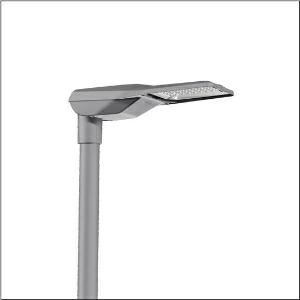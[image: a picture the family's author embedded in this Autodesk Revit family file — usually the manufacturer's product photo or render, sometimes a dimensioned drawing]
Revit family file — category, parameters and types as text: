
# Revit family: streetlight_sl_21_iq_mini___st0_8a_5xe2c31d08jb_69b6
name_source: partatom
category: Lighting Fixtures
units: mm (PartAtom-declared; Revit-internal decimal feet)

## family parameters
Cut with Voids When Loaded = No
Host = Face
Light Source = No
Part Type = Normal
Room Calculation Point = No
Round Connector Dimension = Use Diameter
Shared = No

## types (1)
- --- (1 x LED, 10820 lm, 71.6 W, 3000K)
    Apparent Load = 72 VA
    CIE Flux Codes = 41 75 97 100 100
    Color Rendering = 70
    Color Temperature = 3000K
    Default Elevation = 1800 mm
    Description = Streetlight SL 21 iQ mini, mast luminaire, primary light control with lens, of PMMA, primary optical cover: cover, of toughened safety glass, transparent, light distribution: ST0.8a, light emission: direct distribution, primary light characteristic: asymmetric, installation type: post-top, side-entry, LED, High Power LED, rated luminous flux: 10.820lm, luminous efficacy: 151lm/W, light colour: 730, colour temperature: 3000K, control: Auto-Match, Temp-Guard, Lumen-Switch, Night-Set, Smart-Wire, Light-Fading, Desk-Remote (wireless, voltage-free reading and setting of iQ features in the workshop via application-optimized NFC function/RFID function), optimised constant luminous flux control (CLO 2.0), pre-setting: linear dimming characteristic, mains connection: 220..240V, AC, 50/60Hz, start of lifetime: 72W, end of service life: 75W, reduction: 33W, luminaire housing, of diecast aluminium, powder-coated, Siteco® metallic grey (DB 702S), corrosivity category C5 mid according to DIN EN ISO 12944, please order mast flange separately, inclination adjustable: 0°, 5°, 10°, 15°, sealing non-destructively replaceable, multi-level sealing system, length: 628mm, width: 235mm, height: 110mm, mast flange for spigot size: 42mm (side-entry): 5XC10008XM4, 60/48mm (side-entry/post-top): 5XC10108XM2, 76/60mm (side-entry/post-top): 5XC10108XM1, protection rating (complete): IP66, insulation class (complete): insulation class II (safety insulation), certification: CE, ENEC, ENEC+, VDE, impact resistance: IK09, permissible operating ambient temperature for outdoor applications: -40..+50°C, standard-compliant lighting for roads and squares, packaging unit: 1 piece

Light Distribution: ST0.8a
    Height = 110 mm
    Lamp = 1 x LED
    Lamp Light Flux = 10820 lm
    Lamp Power = 71.6 W
    Lamp count = 1
    Length = 625 mm
    Luminous efficacy = 151 lm/W
    Manufacturer = Siteco
    ModVariant = No
    Model = 5XE2C31D08JB
    Number of Poles = 1
    OnlyDefault = Yes
    Power Factor = 1
    Product Name = Streetlight SL 21 iQ mini | ST0.8a
    Product group = mast luminaire | pylon top
    ProductGroupID = 6100
    Protection Class = Protection class II
    Protection Degree = IP 66
    RLX_Detail_Level = 1
    RLX_Emergency_Light_Flux = 0 lm
    RLX_Emergency_Type = 0
    RLX_Emergency_Type_DB = No
    RlxData = <blob elided: 92337 chars, md5=7be6e93f>
    Socket = socket
    Standby Power = 0 W
    System Light Flux = 10820 lm
    System Power = 72 W
    Type Comments = factory setting: luminous flux: 100 % | dim-lin: 254 | 746 mA
    Type Image = l_1003519.jpg
    URL = http://relux.com
    VarID = @adj_139921
    Voltage = 0 V
    Weight = 0.00 kg
    Width = 234 mm

## geometry (parser evidence)
native form markers: Blend x4, Sweep x12
no freeform markers — native parametric forms only
